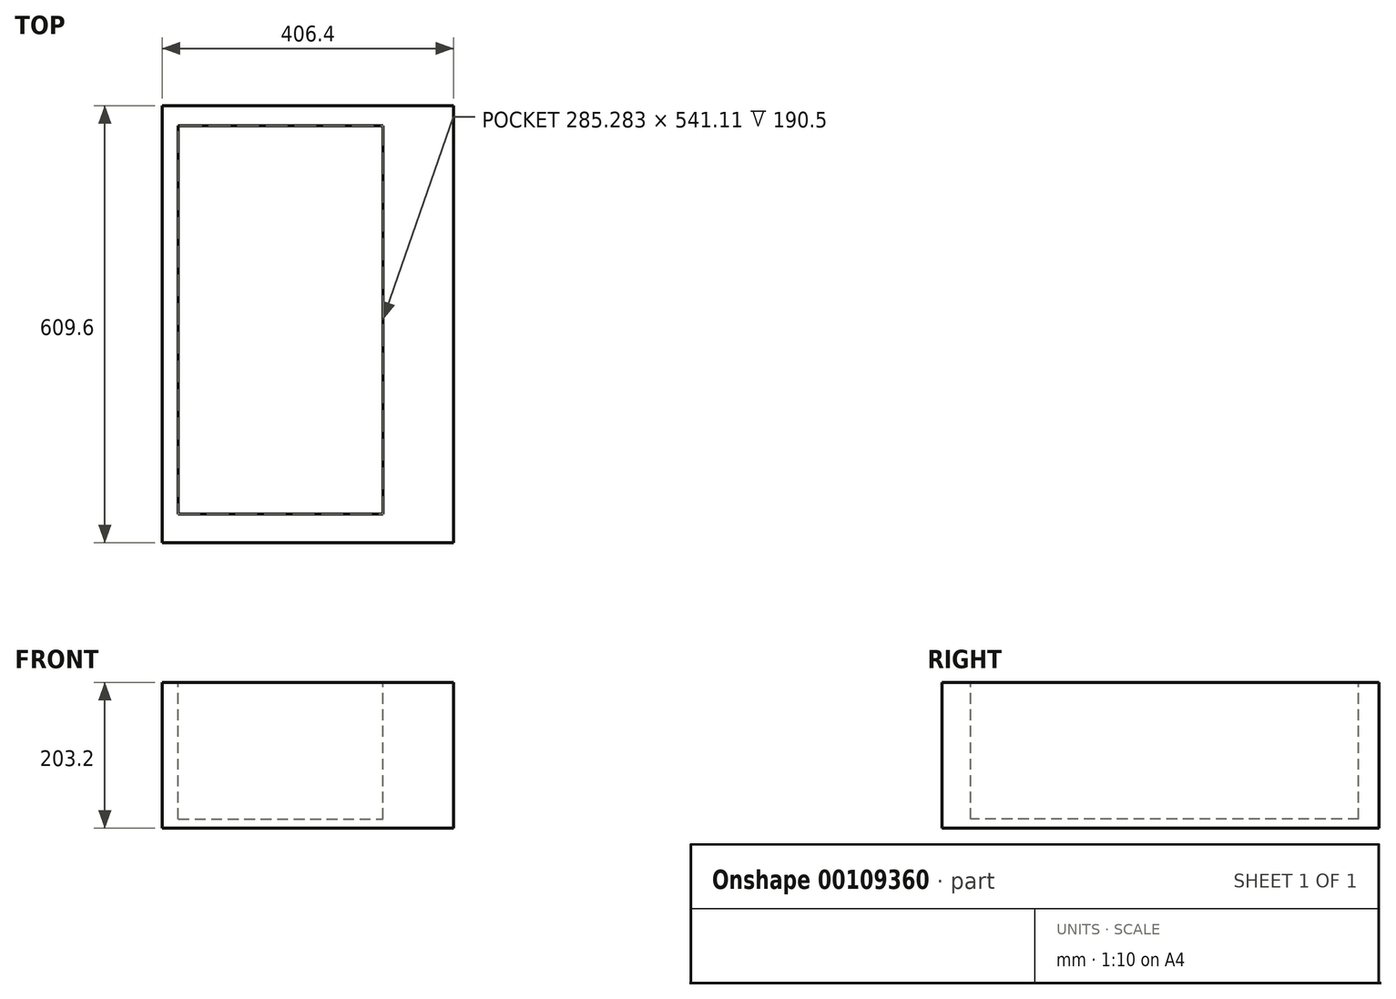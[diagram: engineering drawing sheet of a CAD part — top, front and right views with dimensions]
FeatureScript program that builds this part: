
annotation { "Feature Type Name" : "Feature", "Feature Type Description" : "" }
export const myFeature = defineFeature(function(context is Context, id is Id, definition is map)
    precondition{}
    {
        {
            var Q0;
            Q0=qCreatedBy(makeId("Top.planeOp"),FACE);
            var sketch = newSketch(context, id + "F0", { "sketchPlane" : qUnion([Q0])});
            skLineSegment(sketch, "E0.bottom", {"start": v(203.2, 304.8) * mm, "end": v(-203.2, 304.8) * mm});
            skLineSegment(sketch, "E0.top", {"start": v(203.2, -304.8) * mm, "end": v(-203.2, -304.8) * mm});
            skLineSegment(sketch, "E0.left", {"start": v(203.2, 304.8) * mm, "end": v(203.2, -304.8) * mm});
            skLineSegment(sketch, "E0.right", {"start": v(-203.2, 304.8) * mm, "end": v(-203.2, -304.8) * mm});
            skPoint(sketch, "E0.middle", {"position": v(0, 0) * mm});
            skSolve(sketch);
        }
        {
            var Q0;
            Q0=makeQuery(id+"F0.imprint","IMPRINT",FACE,{"disambiguationData":[TD([[makeQuery(id+"F0.imprint","IMPRINT",EDGE,{"derivedFrom":sQuery(id+"F0.wireOp",EDGE,"E0.bottom")}),1.0]])]});
            extrude(context, id + "F1", {"entities" : qUnion([Q0]), "depth" : 203.2 * mm});
        }
        {
            var Q0;
            Q0=makeQuery(id+"F1.opExtrude","CAP_FACE",FACE,{"disambiguationData":[OSD([sQuery(id+"F0.wireOp",EDGE,"E0.bottom"),sQuery(id+"F0.wireOp",EDGE,"E0.top"),sQuery(id+"F0.wireOp",EDGE,"E0.left"),sQuery(id+"F0.wireOp",EDGE,"E0.right")])],"isStart":false});
            var sketch = newSketch(context, id + "F2", { "sketchPlane" : qUnion([Q0])});
            skLineSegment(sketch, "E1.bottom", {"start": v(-180.66, 276.6) * mm, "end": v(104.62, 276.6) * mm});
            skLineSegment(sketch, "E1.top", {"start": v(-180.66, -264.51) * mm, "end": v(104.62, -264.51) * mm});
            skLineSegment(sketch, "E1.left", {"start": v(-180.66, 276.6) * mm, "end": v(-180.66, -264.51) * mm});
            skLineSegment(sketch, "E1.right", {"start": v(104.62, 276.6) * mm, "end": v(104.62, -264.51) * mm});
            skSolve(sketch);
        }
        {
            var Q0;
            Q0 = qSketchRegion(id + "F2", true);
            extrude(context, id + "F3", {"entities" : qUnion([Q0]), "operationType" : NewBodyOperationType.REMOVE, "oppositeDirection" : true, "depth" : 190.5 * mm});
        }
    });
